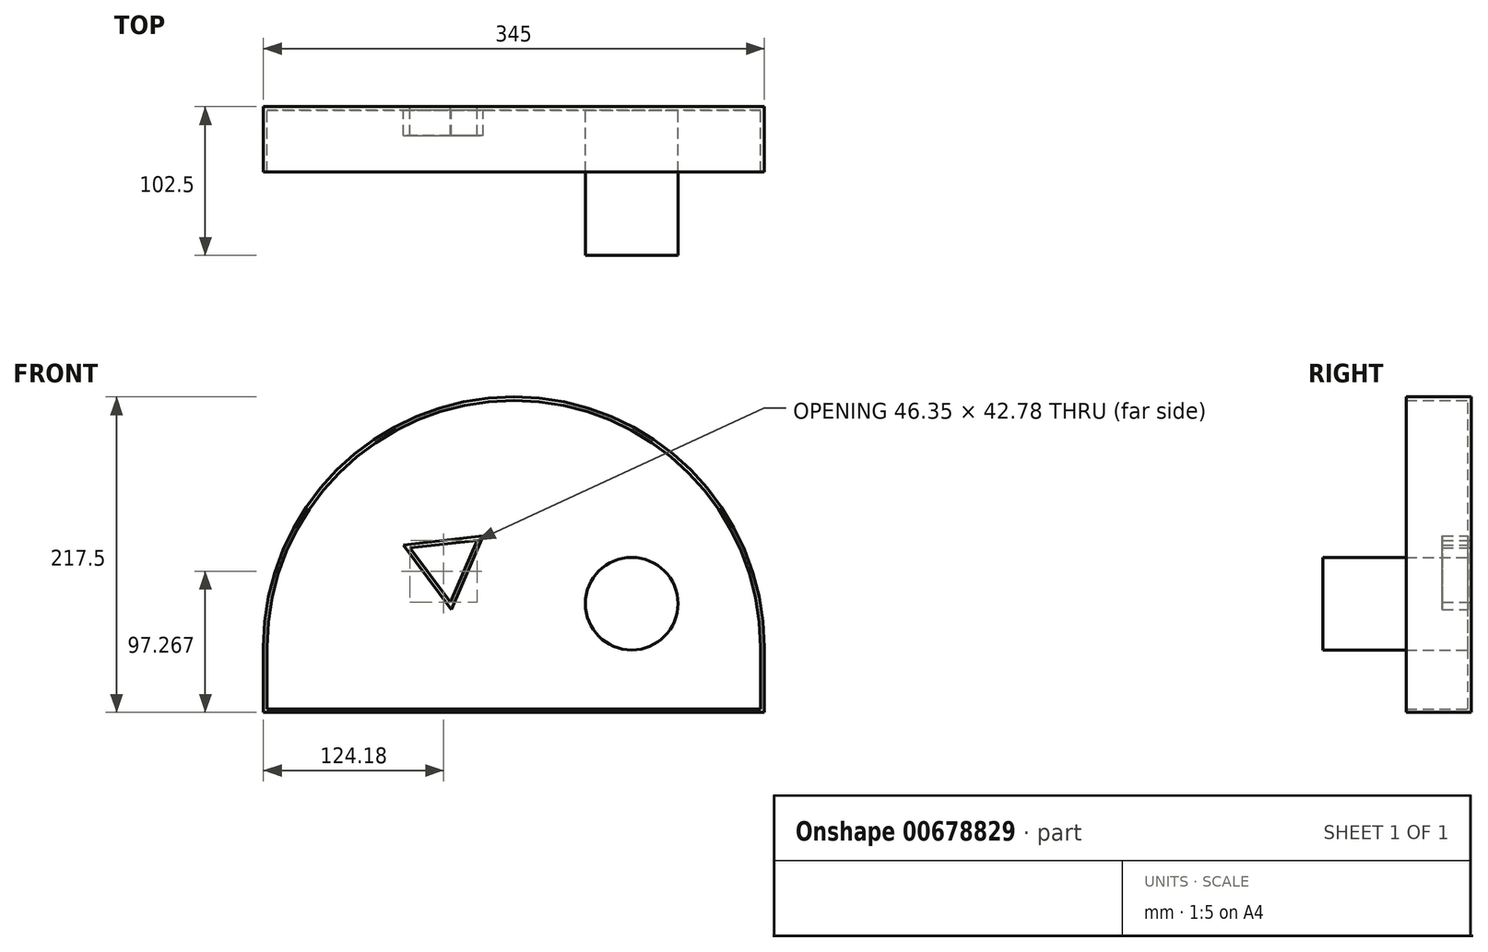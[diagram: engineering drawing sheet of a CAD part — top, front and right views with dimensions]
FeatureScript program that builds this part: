
annotation { "Feature Type Name" : "Feature", "Feature Type Description" : "" }
export const myFeature = defineFeature(function(context is Context, id is Id, definition is map)
    precondition{}
    {
        {
            var Q0;
            Q0=qCreatedBy(makeId("Front.planeOp"),FACE);
            var sketch = newSketch(context, id + "F0", { "sketchPlane" : qUnion([Q0])});
            skLineSegment(sketch, "E0", {"start": v(-253.7, -75) * mm, "end": v(91.3, -75) * mm});
            skLineSegment(sketch, "E1", {"start": v(91.3, -75) * mm, "end": v(91.3, -30) * mm});
            skLineSegment(sketch, "E2", {"start": v(-253.7, -75) * mm, "end": v(-253.7, -30) * mm});
            skArc(sketch, "E3", {"start": v(0, 122.2) * mm, "mid": v(-169.94, 117.93) * mm, "end": v(-253.7, -30) * mm});
            skArc(sketch, "E4", {"start": v(91.3, -30) * mm, "mid": v(66.72, 58.74) * mm, "end": v(0, 122.2) * mm});
            skLineSegment(sketch, "E5.0", {"start": v(-124.97, 0.89) * mm, "end": v(-152.7, 38.4) * mm});
            skLineSegment(sketch, "E5.1", {"start": v(-152.7, 38.4) * mm, "end": v(-106.35, 43.67) * mm});
            skLineSegment(sketch, "E5.2", {"start": v(-106.35, 43.67) * mm, "end": v(-124.97, 0.89) * mm});
            skSolve(sketch);
        }
        {
            var Q0;
            Q0=makeQuery(id+"F0.imprint","IMPRINT",FACE,{"disambiguationData":[TD([[makeQuery(id+"F0.imprint","IMPRINT",EDGE,{"derivedFrom":sQuery(id+"F0.wireOp",EDGE,"E0")}),1.0]])]});
            extrude(context, id + "F1", {"entities" : qUnion([Q0]), "depth" : 45 * mm, "offsetDistance" : 25 * mm});
        }
        {
            var Q0;
            Q0=makeQuery(id+"F1.opExtrude","CAP_FACE",FACE,{"disambiguationData":[OSD([sQuery(id+"F0.wireOp",EDGE,"E0"),sQuery(id+"F0.wireOp",EDGE,"E1"),sQuery(id+"F0.wireOp",EDGE,"E2"),sQuery(id+"F0.wireOp",EDGE,"E3"),sQuery(id+"F0.wireOp",EDGE,"E4")])],"isStart":false});
            shell(context, id + "F2", {"entities" : qUnion([Q0]), "thickness" : 2.5 * mm});
        }
        {
            var Q0;
            Q0=makeQuery(id+"F1.opExtrude","CAP_FACE",FACE,{"disambiguationData":[OSD([sQuery(id+"F0.wireOp",EDGE,"E0"),sQuery(id+"F0.wireOp",EDGE,"E1"),sQuery(id+"F0.wireOp",EDGE,"E2"),sQuery(id+"F0.wireOp",EDGE,"E3"),sQuery(id+"F0.wireOp",EDGE,"E4"),sQuery(id+"F0.wireOp",EDGE,"E5.0"),sQuery(id+"F0.wireOp",EDGE,"E5.1"),sQuery(id+"F0.wireOp",EDGE,"E5.2")])],"isStart":false});
            extrude(context, id + "F3", {"entities" : qUnion([Q0]), "operationType" : NewBodyOperationType.REMOVE, "oppositeDirection" : true, "depth" : 25 * mm, "offsetDistance" : 25 * mm});
        }
        {
            var Q0;
            {var subQ0=sQuery(id+"F0.wireOp",EDGE,"E5.2");var subQ1=sQuery(id+"F0.wireOp",EDGE,"E5.1");var subQ2=sQuery(id+"F0.wireOp",EDGE,"E5.0");var subQ3=sQuery(id+"F0.wireOp",EDGE,"E4");var subQ4=sQuery(id+"F0.wireOp",EDGE,"E3");var subQ5=sQuery(id+"F0.wireOp",EDGE,"E2");var subQ6=sQuery(id+"F0.wireOp",EDGE,"E1");var subQ7=sQuery(id+"F0.wireOp",EDGE,"E0");Q0=makeQuery(id+"F2.opShell","OFFSET_FACE",FACE,{"disambiguationData":[OSD([subQ7,subQ6,subQ5,subQ4,subQ3,subQ2,subQ1,subQ0]),TDD([makeQuery(id+"F1.opExtrude","CAP_FACE",FACE,{"disambiguationData":[OSD([subQ7,subQ6,subQ5,subQ4,subQ3,subQ2,subQ1,subQ0])],"isStart":true})])]});}
            var sketch = newSketch(context, id + "F4", { "sketchPlane" : qUnion([Q0])});
            skCircle(sketch, "E6", {"center": v(0, 0) * mm, "radius": 31.89 * mm});
            skSolve(sketch);
        }
        {
            var Q0;
            Q0=makeQuery(id+"F4.imprint","IMPRINT",FACE,{"disambiguationData":[TD([[makeQuery(id+"F4.imprint","IMPRINT",EDGE,{"derivedFrom":sQuery(id+"F4.wireOp",EDGE,"E6")}),1.0]])]});
            extrude(context, id + "F5", {"entities" : qUnion([Q0]), "operationType" : NewBodyOperationType.ADD, "depth" : 100 * mm, "offsetDistance" : 25 * mm});
        }
    });
